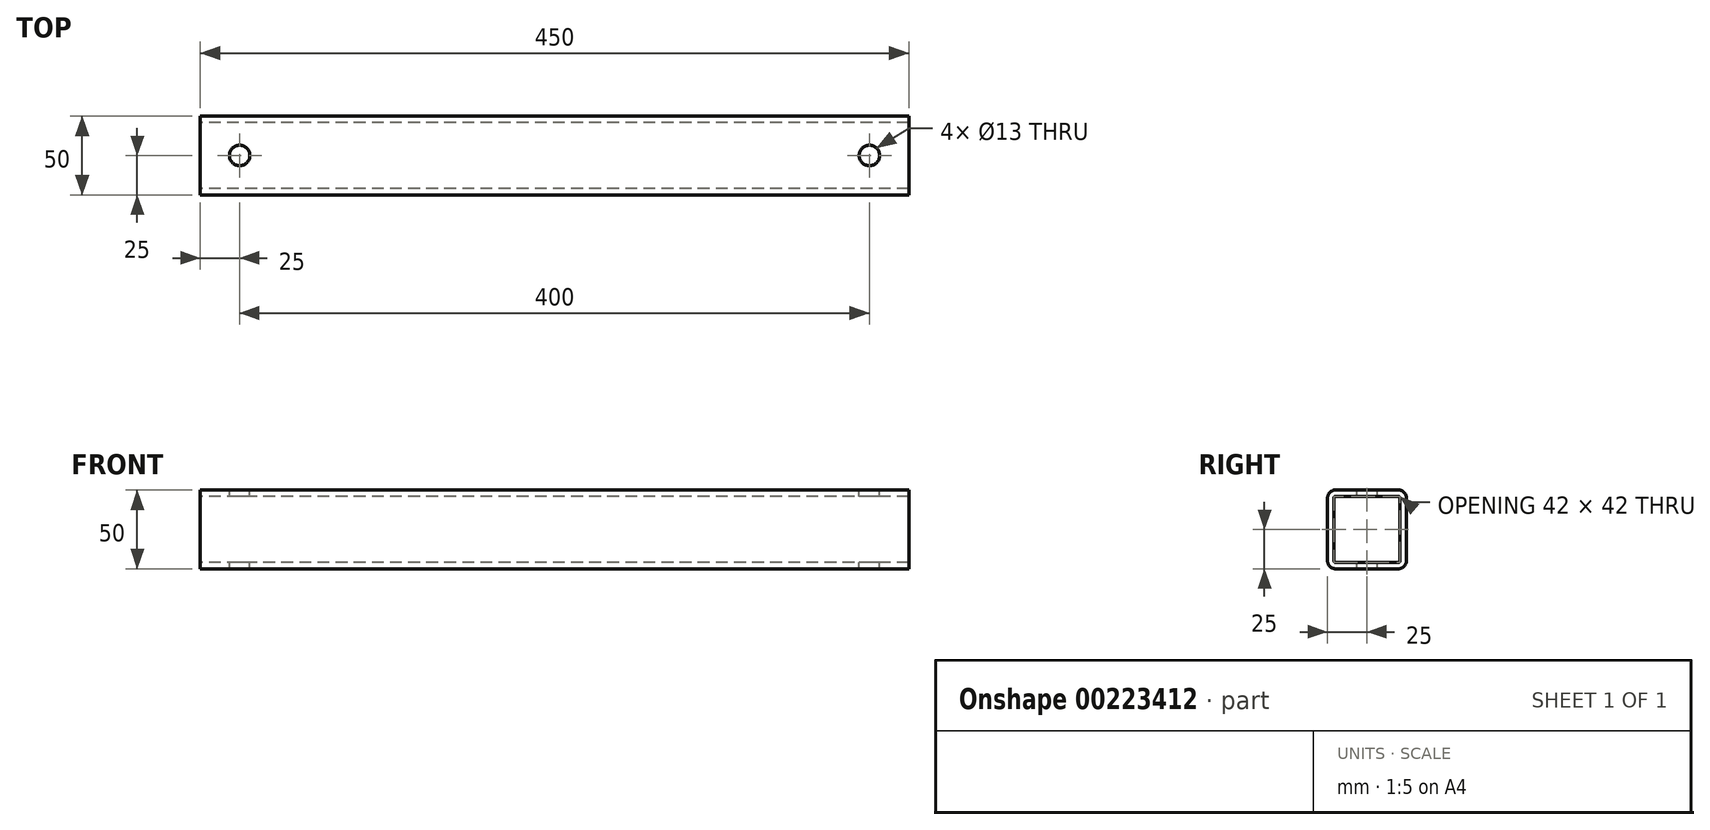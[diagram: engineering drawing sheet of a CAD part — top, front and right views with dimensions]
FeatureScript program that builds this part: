
annotation { "Feature Type Name" : "Feature", "Feature Type Description" : "" }
export const myFeature = defineFeature(function(context is Context, id is Id, definition is map)
    precondition{}
    {
        {
            var Q0;
            Q0=qCreatedBy(makeId("Right.planeOp"),FACE);
            var sketch = newSketch(context, id + "F0", { "sketchPlane" : qUnion([Q0])});
            skLineSegment(sketch, "E0.bottom", {"start": v(5, 0) * mm, "end": v(45, 0) * mm});
            skLineSegment(sketch, "E0.top", {"start": v(5, 50) * mm, "end": v(45, 50) * mm});
            skLineSegment(sketch, "E0.left", {"start": v(0, 5) * mm, "end": v(0, 45) * mm});
            skLineSegment(sketch, "E0.right", {"start": v(50, 5) * mm, "end": v(50, 45) * mm});
            skPoint(sketch, "E1.visualSharp", {"position": v(0, 50) * mm});
            skArc(sketch, "E1.filletArc", {"start": v(5, 50) * mm, "mid": v(1.46, 48.54) * mm, "end": v(0, 45) * mm});
            skPoint(sketch, "E2.visualSharp", {"position": v(50, 50) * mm});
            skArc(sketch, "E2.filletArc", {"start": v(50, 45) * mm, "mid": v(48.54, 48.54) * mm, "end": v(45, 50) * mm});
            skPoint(sketch, "E3.visualSharp", {"position": v(50, 0) * mm});
            skArc(sketch, "E3.filletArc", {"start": v(45, 0) * mm, "mid": v(48.54, 1.46) * mm, "end": v(50, 5) * mm});
            skPoint(sketch, "E4.visualSharp", {"position": v(0, 0) * mm});
            skArc(sketch, "E4.filletArc", {"start": v(0, 5) * mm, "mid": v(1.46, 1.46) * mm, "end": v(5, 0) * mm});
            skLineSegment(sketch, "E5.0", {"start": v(5, 4) * mm, "end": v(45, 4) * mm});
            skArc(sketch, "E5.1", {"start": v(4, 5) * mm, "mid": v(4.3, 4.3) * mm, "end": v(5, 4) * mm});
            skArc(sketch, "E5.2", {"start": v(45, 4) * mm, "mid": v(45.7, 4.3) * mm, "end": v(46, 5) * mm});
            skLineSegment(sketch, "E5.3", {"start": v(4, 5) * mm, "end": v(4, 45) * mm});
            skLineSegment(sketch, "E5.4", {"start": v(46, 5) * mm, "end": v(46, 45) * mm});
            skArc(sketch, "E5.5", {"start": v(46, 45) * mm, "mid": v(45.7, 45.7) * mm, "end": v(45, 46) * mm});
            skLineSegment(sketch, "E5.6", {"start": v(5, 46) * mm, "end": v(45, 46) * mm});
            skArc(sketch, "E5.7", {"start": v(5, 46) * mm, "mid": v(4.3, 45.7) * mm, "end": v(4, 45) * mm});
            skSolve(sketch);
        }
        {
            var Q0;
            Q0=makeQuery(id+"F0.imprint","IMPRINT",FACE,{"disambiguationData":[TD([[makeQuery(id+"F0.imprint","IMPRINT",EDGE,{"derivedFrom":sQuery(id+"F0.wireOp",EDGE,"E0.bottom")}),1.0]])]});
            extrude(context, id + "F1", {"entities" : qUnion([Q0]), "depth" : 450 * mm});
        }
        {
            var Q0;
            Q0=makeQuery(id+"F1.opExtrude","SWEPT_FACE",FACE,{"disambiguationData":[OSD([sQuery(id+"F0.wireOp",EDGE,"E0.top")])]});
            var sketch = newSketch(context, id + "F2", { "sketchPlane" : qUnion([Q0])});
            skCircle(sketch, "E6", {"center": v(25, 25) * mm, "radius": 6.5 * mm});
            skPoint(sketch, "E6.centerSnap0", {"position": v(0, 25) * mm});
            skCircle(sketch, "E7", {"center": v(425, 25) * mm, "radius": 6.5 * mm});
            skPoint(sketch, "E7.centerSnap0", {"position": v(450, 25) * mm});
            skSolve(sketch);
        }
        {
            var Q0;
            Q0=makeQuery(id+"F2.imprint","IMPRINT",FACE,{"disambiguationData":[TD([[makeQuery(id+"F2.imprint","IMPRINT",EDGE,{"derivedFrom":sQuery(id+"F2.wireOp",EDGE,"E6")}),1.0]])]});
            var Q1;
            Q1=makeQuery(id+"F2.imprint","IMPRINT",FACE,{"disambiguationData":[TD([[makeQuery(id+"F2.imprint","IMPRINT",EDGE,{"derivedFrom":sQuery(id+"F2.wireOp",EDGE,"E7")}),1.0]])]});
            extrude(context, id + "F3", {"entities" : qUnion([Q0, Q1]), "operationType" : NewBodyOperationType.REMOVE, "endBound" : BoundingType.THROUGH_ALL, "oppositeDirection" : true, "depth" : 25 * mm});
        }
    });
